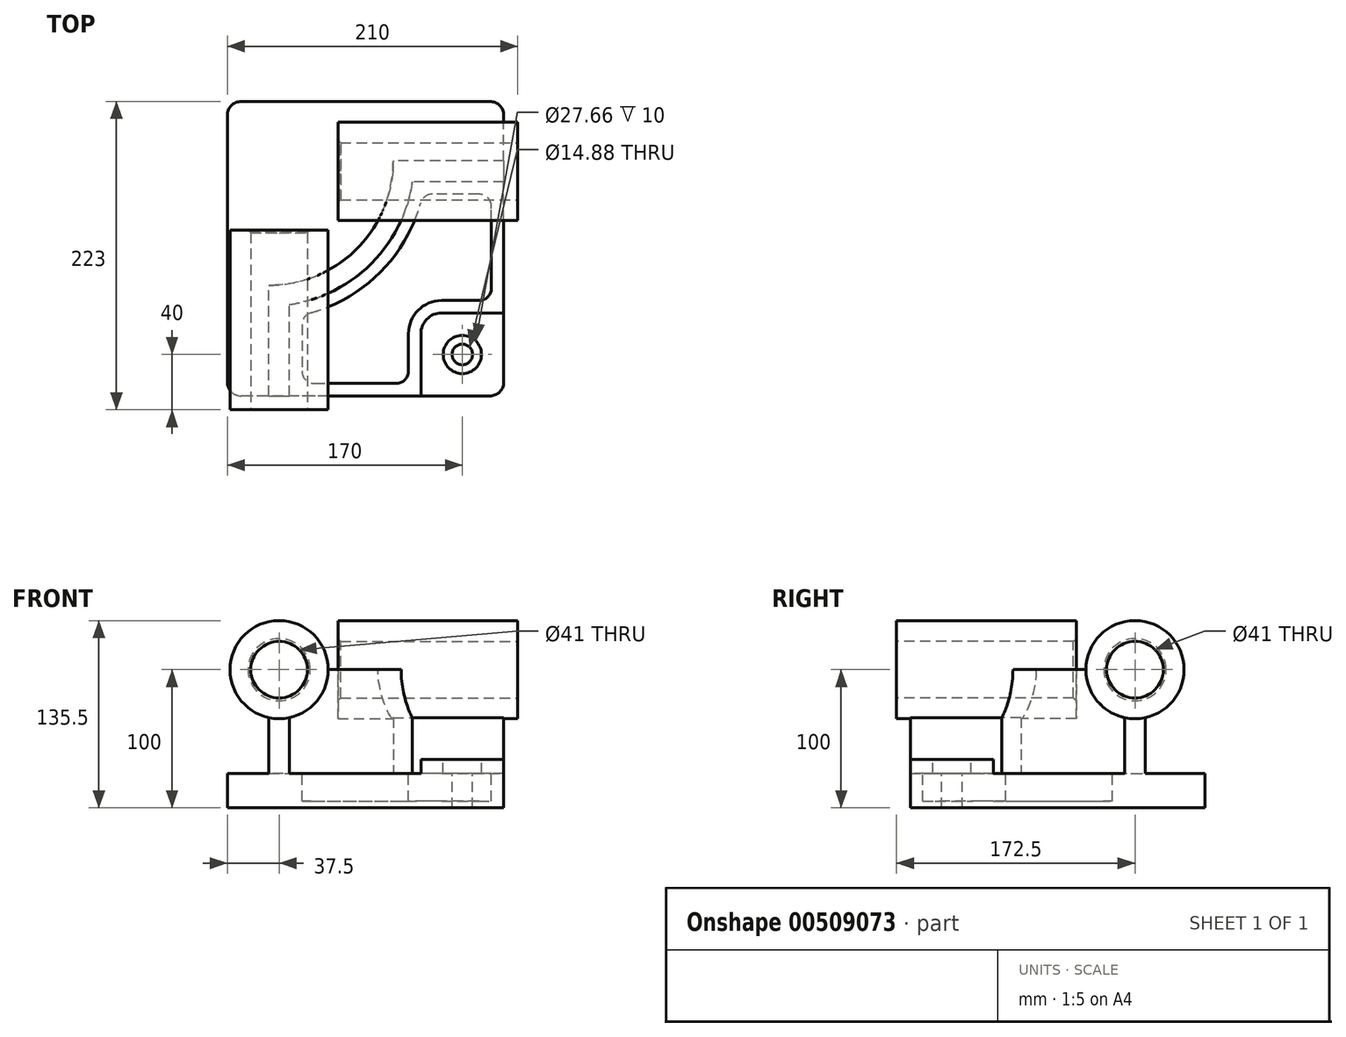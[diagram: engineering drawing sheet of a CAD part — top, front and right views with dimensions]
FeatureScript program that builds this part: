
annotation { "Feature Type Name" : "Feature", "Feature Type Description" : "" }
export const myFeature = defineFeature(function(context is Context, id is Id, definition is map)
    precondition{}
    {
        {
            var Q0;
            Q0=qCreatedBy(makeId("Top.planeOp"),FACE);
            var sketch = newSketch(context, id + "F0", { "sketchPlane" : qUnion([Q0])});
            skLineSegment(sketch, "E0.bottom", {"start": v(-10, 0) * mm, "end": v(-190, 0) * mm});
            skLineSegment(sketch, "E0.top", {"start": v(-10, 213) * mm, "end": v(-190, 213) * mm});
            skLineSegment(sketch, "E0.left", {"start": v(0, 10) * mm, "end": v(0, 203) * mm});
            skLineSegment(sketch, "E0.right", {"start": v(-200, 10) * mm, "end": v(-200, 203) * mm});
            skPoint(sketch, "E1.visualSharp", {"position": v(-200, 213) * mm});
            skArc(sketch, "E1.filletArc", {"start": v(-190, 213) * mm, "mid": v(-197.07, 210.07) * mm, "end": v(-200, 203) * mm});
            skPoint(sketch, "E2.visualSharp", {"position": v(0, 213) * mm});
            skArc(sketch, "E2.filletArc", {"start": v(0, 203) * mm, "mid": v(-2.93, 210.07) * mm, "end": v(-10, 213) * mm});
            skPoint(sketch, "E3.visualSharp", {"position": v(0, 0) * mm});
            skArc(sketch, "E3.filletArc", {"start": v(-10, 0) * mm, "mid": v(-2.93, 2.93) * mm, "end": v(0, 10) * mm});
            skPoint(sketch, "E4.visualSharp", {"position": v(-200, 0) * mm});
            skArc(sketch, "E4.filletArc", {"start": v(-200, 10) * mm, "mid": v(-197.07, 2.93) * mm, "end": v(-190, 0) * mm});
            skSolve(sketch);
        }
        {
            var Q0;
            Q0=makeQuery(id+"F0.imprint","IMPRINT",FACE,{"disambiguationData":[TD([[makeQuery(id+"F0.imprint","IMPRINT",EDGE,{"derivedFrom":sQuery(id+"F0.wireOp",EDGE,"E0.bottom")}),-1.0]])]});
            extrude(context, id + "F1", {"entities" : qUnion([Q0]), "depth" : 25 * mm});
        }
        {
            var Q0;
            Q0=makeQuery(id+"F1.opExtrude","CAP_FACE",FACE,{"disambiguationData":[OSD([sQuery(id+"F0.wireOp",EDGE,"E0.bottom"),sQuery(id+"F0.wireOp",EDGE,"E0.top"),sQuery(id+"F0.wireOp",EDGE,"E0.left"),sQuery(id+"F0.wireOp",EDGE,"E0.right"),sQuery(id+"F0.wireOp",EDGE,"E1.filletArc"),sQuery(id+"F0.wireOp",EDGE,"E2.filletArc"),sQuery(id+"F0.wireOp",EDGE,"E3.filletArc"),sQuery(id+"F0.wireOp",EDGE,"E4.filletArc")])],"isStart":false});
            var sketch = newSketch(context, id + "F2", { "sketchPlane" : qUnion([Q0])});
            skLineSegment(sketch, "E5", {"start": v(0, 170) * mm, "end": v(-80, 170) * mm});
            skLineSegment(sketch, "E6", {"start": v(-170, 0) * mm, "end": v(-170, 80) * mm});
            skLineSegment(sketch, "E7.0", {"start": v(0, 155) * mm, "end": v(-66.08, 155) * mm});
            skLineSegment(sketch, "E8.0", {"start": v(-155, 0) * mm, "end": v(-155, 66.08) * mm});
            skLineSegment(sketch, "E9", {"start": v(-170, 80) * mm, "end": v(-170, 170) * mm, "construction": true});
            skLineSegment(sketch, "E10", {"start": v(-170, 170) * mm, "end": v(-80, 170) * mm, "construction": true});
            skArc(sketch, "E11", {"start": v(-170, 80) * mm, "mid": v(-106.36, 106.36) * mm, "end": v(-80, 170) * mm});
            skArc(sketch, "E12", {"start": v(-155, 66.08) * mm, "mid": v(-95.75, 95.75) * mm, "end": v(-66.08, 155) * mm});
            skSolve(sketch);
        }
        {
            var Q0;
            Q0 = qSketchRegion(id + "F2", true);
            var Q1;
            {var subQ4=sQuery(id+"F2.wireOp",EDGE,"E5");Q1=makeQuery(id+"F2.imprint","IMPRINT",FACE,{"disambiguationData":[TD([[makeQuery(id+"F2.imprint","IMPRINT",EDGE,{"derivedFrom":subQ4}),1.0]])]});}
            extrude(context, id + "F3", {"entities" : qUnion([Q0, Q1]), "operationType" : NewBodyOperationType.ADD, "depth" : 75 * mm});
        }
        {
            var Q0;
            {var subQ0=sQuery(id+"F0.wireOp",EDGE,"E3.filletArc");var subQ1=sQuery(id+"F0.wireOp",EDGE,"E0.left");var subQ2=sQuery(id+"F0.wireOp",EDGE,"E0.bottom");Q0=makeQuery(id+"F3.boolean.opBoolean","SPLIT",FACE,{"disambiguationData":[TD([makeQuery(id+"F1.opExtrude","SWEPT_FACE",FACE,{"disambiguationData":[OSD([subQ0])]})])],"derivedFrom":makeQuery(id+"F1.opExtrude","CAP_FACE",FACE,{"disambiguationData":[OSD([subQ2,sQuery(id+"F0.wireOp",EDGE,"E0.top"),subQ1,sQuery(id+"F0.wireOp",EDGE,"E0.right"),sQuery(id+"F0.wireOp",EDGE,"E1.filletArc"),sQuery(id+"F0.wireOp",EDGE,"E2.filletArc"),subQ0,sQuery(id+"F0.wireOp",EDGE,"E4.filletArc")])],"isStart":false})});}
            var sketch = newSketch(context, id + "F4", { "sketchPlane" : qUnion([Q0])});
            skLineSegment(sketch, "E13.bottom", {"start": v(-45, 60) * mm, "end": v(0, 60) * mm});
            skLineSegment(sketch, "E13.top", {"start": v(-60, 0) * mm, "end": v(-10, 0) * mm});
            skLineSegment(sketch, "E13.left", {"start": v(-60, 45) * mm, "end": v(-60, 0) * mm});
            skLineSegment(sketch, "E13.right", {"start": v(0, 60) * mm, "end": v(0, 10) * mm});
            skPoint(sketch, "E14.visualSharp", {"position": v(0, 0) * mm});
            skArc(sketch, "E14.filletArc", {"start": v(-10, 0) * mm, "mid": v(-2.93, 2.93) * mm, "end": v(0, 10) * mm});
            skPoint(sketch, "E15.visualSharp", {"position": v(-60, 60) * mm});
            skArc(sketch, "E15.filletArc", {"start": v(-45, 60) * mm, "mid": v(-55.6, 55.6) * mm, "end": v(-60, 45) * mm});
            skSolve(sketch);
        }
        {
            var Q0;
            Q0=makeQuery(id+"F4.imprint","IMPRINT",FACE,{"disambiguationData":[TD([[makeQuery(id+"F4.imprint","IMPRINT",EDGE,{"derivedFrom":sQuery(id+"F4.wireOp",EDGE,"E13.bottom")}),-1.0]])]});
            extrude(context, id + "F5", {"entities" : qUnion([Q0]), "operationType" : NewBodyOperationType.ADD, "depth" : 10 * mm});
        }
        {
            var Q0;
            Q0=makeQuery(id+"F5.opExtrude","CAP_FACE",FACE,{"disambiguationData":[OSD([sQuery(id+"F4.wireOp",EDGE,"E13.bottom"),sQuery(id+"F4.wireOp",EDGE,"E13.top"),sQuery(id+"F4.wireOp",EDGE,"E13.left"),sQuery(id+"F4.wireOp",EDGE,"E13.right"),sQuery(id+"F4.wireOp",EDGE,"E14.filletArc"),sQuery(id+"F4.wireOp",EDGE,"E15.filletArc")])],"isStart":false});
            var sketch = newSketch(context, id + "F6", { "sketchPlane" : qUnion([Q0])});
            skSolve(sketch);
        }
        {
            var Q0;
            Q0=makeQuery(id+"F6.imprint","IMPRINT",FACE,{"disambiguationData":[TD([[makeQuery(id+"F6.imprint","IMPRINT",EDGE,{"derivedFrom":makeQuery(id+"F5.opExtrude","CAP_EDGE",EDGE,{"disambiguationData":[OSD([sQuery(id+"F4.wireOp",EDGE,"E13.bottom")])],"isStart":false})}),-1.0]])]});
            var sketch = newSketch(context, id + "F7", { "sketchPlane" : qUnion([Q0])});
            skCircle(sketch, "E16", {"center": v(-30, 30) * mm, "radius": 13.83 * mm});
            skCircle(sketch, "E17", {"center": v(-30, 30) * mm, "radius": 7.44 * mm});
            skSolve(sketch);
        }
        {
            var Q0;
            Q0 = qSketchRegion(id + "F7", true);
            extrude(context, id + "F8", {"entities" : qUnion([Q0]), "operationType" : NewBodyOperationType.REMOVE, "oppositeDirection" : true, "depth" : 10 * mm});
        }
        {
            var Q0;
            Q0=makeQuery(id+"F7.imprint","IMPRINT",FACE,{"disambiguationData":[TD([[makeQuery(id+"F7.imprint","IMPRINT",EDGE,{"derivedFrom":sQuery(id+"F7.wireOp",EDGE,"E17")}),1.0]])]});
            var Q1;
            Q1=sQuery(id+"F7.wireOp",EDGE,"E17");
            extrude(context, id + "F9", {"entities" : qUnion([Q0]), "operationType" : NewBodyOperationType.REMOVE, "surfaceEntities" : qUnion([Q1]), "endBound" : BoundingType.THROUGH_ALL, "oppositeDirection" : true, "depth" : 25 * mm});
        }
        {
            var Q0;
            {var subQ0=sQuery(id+"F0.wireOp",EDGE,"E3.filletArc");var subQ1=sQuery(id+"F0.wireOp",EDGE,"E0.left");var subQ2=sQuery(id+"F0.wireOp",EDGE,"E0.bottom");Q0=makeQuery(id+"F3.boolean.opBoolean","SPLIT",FACE,{"disambiguationData":[TD([makeQuery(id+"F1.opExtrude","SWEPT_FACE",FACE,{"disambiguationData":[OSD([subQ0])]})])],"derivedFrom":makeQuery(id+"F1.opExtrude","CAP_FACE",FACE,{"disambiguationData":[OSD([subQ2,sQuery(id+"F0.wireOp",EDGE,"E0.top"),subQ1,sQuery(id+"F0.wireOp",EDGE,"E0.right"),sQuery(id+"F0.wireOp",EDGE,"E1.filletArc"),sQuery(id+"F0.wireOp",EDGE,"E2.filletArc"),subQ0,sQuery(id+"F0.wireOp",EDGE,"E4.filletArc")])],"isStart":false})});}
            var sketch = newSketch(context, id + "F10", { "sketchPlane" : qUnion([Q0])});
            skArc(sketch, "E18.0.0", {"start": v(-60, 45) * mm, "mid": v(-55.6, 55.6) * mm, "end": v(-45, 60) * mm});
            skLineSegment(sketch, "E18.0.1", {"start": v(-45, 60) * mm, "end": v(0, 60) * mm});
            skLineSegment(sketch, "E18.0.2", {"start": v(0, 60) * mm, "end": v(0, 155) * mm});
            skLineSegment(sketch, "E18.0.3", {"start": v(0, 155) * mm, "end": v(-66.08, 155) * mm});
            skArc(sketch, "E18.0.4", {"start": v(-66.08, 155) * mm, "mid": v(-95.75, 95.75) * mm, "end": v(-155, 66.08) * mm});
            skLineSegment(sketch, "E18.0.5", {"start": v(-155, 66.08) * mm, "end": v(-155, 0) * mm});
            skLineSegment(sketch, "E18.0.6", {"start": v(-155, 0) * mm, "end": v(-60, 0) * mm});
            skLineSegment(sketch, "E18.0.7", {"start": v(-60, 0) * mm, "end": v(-60, 45) * mm});
            skLineSegment(sketch, "E19.0", {"start": v(-69, 18) * mm, "end": v(-69, 45) * mm});
            skLineSegment(sketch, "E19.1", {"start": v(-137, 9) * mm, "end": v(-78, 9) * mm});
            skArc(sketch, "E19.2", {"start": v(-69, 45) * mm, "mid": v(-61.97, 61.97) * mm, "end": v(-45, 69) * mm});
            skLineSegment(sketch, "E19.3", {"start": v(-146, 51.5) * mm, "end": v(-146, 18) * mm});
            skLineSegment(sketch, "E19.4", {"start": v(-45, 69) * mm, "end": v(-18, 69) * mm});
            skLineSegment(sketch, "E19.5", {"start": v(-9, 78) * mm, "end": v(-9, 137) * mm});
            skLineSegment(sketch, "E19.6", {"start": v(-18, 146) * mm, "end": v(-51.5, 146) * mm});
            skArc(sketch, "E19.7", {"start": v(-60.18, 139.41) * mm, "mid": v(-89.39, 89.39) * mm, "end": v(-139.41, 60.18) * mm});
            skPoint(sketch, "E20.visualSharp", {"position": v(-146, 58.55) * mm});
            skArc(sketch, "E20.filletArc", {"start": v(-139.41, 60.18) * mm, "mid": v(-144.17, 56.95) * mm, "end": v(-146, 51.5) * mm});
            skPoint(sketch, "E21.visualSharp", {"position": v(-146, 9) * mm});
            skArc(sketch, "E21.filletArc", {"start": v(-146, 18) * mm, "mid": v(-143.36, 11.64) * mm, "end": v(-137, 9) * mm});
            skPoint(sketch, "E22.visualSharp", {"position": v(-69, 9) * mm});
            skArc(sketch, "E22.filletArc", {"start": v(-78, 9) * mm, "mid": v(-71.64, 11.64) * mm, "end": v(-69, 18) * mm});
            skPoint(sketch, "E23.visualSharp", {"position": v(-9, 69) * mm});
            skArc(sketch, "E23.filletArc", {"start": v(-18, 69) * mm, "mid": v(-11.64, 71.64) * mm, "end": v(-9, 78) * mm});
            skPoint(sketch, "E24.visualSharp", {"position": v(-9, 146) * mm});
            skArc(sketch, "E24.filletArc", {"start": v(-9, 137) * mm, "mid": v(-11.64, 143.36) * mm, "end": v(-18, 146) * mm});
            skPoint(sketch, "E25.visualSharp", {"position": v(-58.55, 146) * mm});
            skArc(sketch, "E25.filletArc", {"start": v(-51.5, 146) * mm, "mid": v(-56.95, 144.17) * mm, "end": v(-60.18, 139.41) * mm});
            skSolve(sketch);
        }
        {
            var Q0;
            Q0=makeQuery(id+"F10.imprint","IMPRINT",FACE,{"disambiguationData":[TD([[makeQuery(id+"F10.imprint","IMPRINT",EDGE,{"derivedFrom":sQuery(id+"F10.wireOp",EDGE,"E19.0")}),1.0]])]});
            extrude(context, id + "F11", {"entities" : qUnion([Q0]), "operationType" : NewBodyOperationType.REMOVE, "oppositeDirection" : true, "depth" : 20 * mm});
        }
        {
            var Q0;
            {var subQ0=sQuery(id+"F0.wireOp",EDGE,"E0.bottom");Q0=makeQuery(id+"F5.boolean.opBoolean","MERGE",FACE,{"derivedFrom":[makeQuery(id+"F3.boolean.opBoolean","MERGE",FACE,{"derivedFrom":[makeQuery(id+"F1.opExtrude","SWEPT_FACE",FACE,{"disambiguationData":[OSD([subQ0])]}),makeQuery(id+"F3.opExtrude","SWEPT_FACE",FACE,{"disambiguationData":[OSD([subQ0])]})]}),makeQuery(id+"F5.opExtrude","SWEPT_FACE",FACE,{"disambiguationData":[OSD([sQuery(id+"F4.wireOp",EDGE,"E13.top")])]})]});}
            cPlane(context, id + "F12", {"entities" : qUnion([Q0]), "cplaneType" : CPlaneType.OFFSET, "offset" : 10 * mm, "width" : 150 * mm, "height" : 150 * mm});
        }
        {
            var Q0;
            Q0=qCreatedBy(id+"F12.planeOp",FACE);
            var sketch = newSketch(context, id + "F13", { "sketchPlane" : qUnion([Q0])});
            skCircle(sketch, "E26", {"center": v(-162.5, 100) * mm, "radius": 35.5 * mm});
            skSolve(sketch);
        }
        {
            var Q0;
            Q0=makeQuery(id+"F13.imprint","IMPRINT",FACE,{"disambiguationData":[TD([[makeQuery(id+"F13.imprint","IMPRINT",EDGE,{"derivedFrom":sQuery(id+"F13.wireOp",EDGE,"E26")}),1.0]])]});
            extrude(context, id + "F14", {"entities" : qUnion([Q0]), "operationType" : NewBodyOperationType.ADD, "oppositeDirection" : true, "depth" : 130 * mm});
        }
        {
            var Q0;
            Q0=makeQuery(id+"F14.opExtrude","CAP_FACE",FACE,{"disambiguationData":[OSD([sQuery(id+"F13.wireOp",EDGE,"E26")])],"isStart":true});
            var sketch = newSketch(context, id + "F15", { "sketchPlane" : qUnion([Q0])});
            skCircle(sketch, "E27", {"center": v(-162.5, 100) * mm, "radius": 20.5 * mm});
            skSolve(sketch);
        }
        {
            var Q0;
            Q0 = qSketchRegion(id + "F15", true);
            extrude(context, id + "F16", {"entities" : qUnion([Q0]), "operationType" : NewBodyOperationType.REMOVE, "endBound" : BoundingType.THROUGH_ALL, "oppositeDirection" : true, "depth" : 25 * mm});
        }
        {
            var Q0;
            {var subQ0=sQuery(id+"F0.wireOp",EDGE,"E0.left");Q0=makeQuery(id+"F5.boolean.opBoolean","MERGE",FACE,{"derivedFrom":[makeQuery(id+"F3.boolean.opBoolean","MERGE",FACE,{"derivedFrom":[makeQuery(id+"F1.opExtrude","SWEPT_FACE",FACE,{"disambiguationData":[OSD([subQ0])]}),makeQuery(id+"F3.opExtrude","SWEPT_FACE",FACE,{"disambiguationData":[OSD([subQ0])]})]}),makeQuery(id+"F5.opExtrude","SWEPT_FACE",FACE,{"disambiguationData":[OSD([sQuery(id+"F4.wireOp",EDGE,"E13.right")])]})]});}
            cPlane(context, id + "F17", {"entities" : qUnion([Q0]), "cplaneType" : CPlaneType.OFFSET, "offset" : 10 * mm, "width" : 150 * mm, "height" : 150 * mm});
        }
        {
            var Q0;
            Q0=qCreatedBy(id+"F17.planeOp",FACE);
            var sketch = newSketch(context, id + "F18", { "sketchPlane" : qUnion([Q0])});
            skCircle(sketch, "E28", {"center": v(162.5, 100) * mm, "radius": 35.5 * mm});
            skSolve(sketch);
        }
        {
            var Q0;
            Q0=makeQuery(id+"F18.imprint","IMPRINT",FACE,{"disambiguationData":[TD([[makeQuery(id+"F18.imprint","IMPRINT",EDGE,{"derivedFrom":sQuery(id+"F18.wireOp",EDGE,"E28")}),1.0]])]});
            extrude(context, id + "F19", {"entities" : qUnion([Q0]), "operationType" : NewBodyOperationType.ADD, "oppositeDirection" : true, "depth" : 130 * mm});
        }
        {
            var Q0;
            Q0=makeQuery(id+"F19.opExtrude","CAP_FACE",FACE,{"disambiguationData":[OSD([sQuery(id+"F18.wireOp",EDGE,"E28")])],"isStart":true});
            var sketch = newSketch(context, id + "F20", { "sketchPlane" : qUnion([Q0])});
            skCircle(sketch, "E29", {"center": v(162.5, 100) * mm, "radius": 20.5 * mm});
            skSolve(sketch);
        }
        {
            var Q0;
            Q0=makeQuery(id+"F20.imprint","IMPRINT",FACE,{"disambiguationData":[TD([[makeQuery(id+"F20.imprint","IMPRINT",EDGE,{"derivedFrom":sQuery(id+"F20.wireOp",EDGE,"E29")}),1.0]])]});
            var Q1;
            Q1=sQuery(id+"F20.wireOp",EDGE,"E29");
            extrude(context, id + "F21", {"entities" : qUnion([Q0]), "operationType" : NewBodyOperationType.REMOVE, "surfaceEntities" : qUnion([Q1]), "endBound" : BoundingType.THROUGH_ALL, "oppositeDirection" : true, "depth" : 25 * mm});
        }
        {
            var Q0;
            Q0=makeQuery(id+"F21.boolean.opBoolean","COPY",EDGE,{"derivedFrom":makeQuery(id+"F21.opExtrude","CAP_EDGE",EDGE,{"disambiguationData":[OSD([sQuery(id+"F20.wireOp",EDGE,"E29")])],"isStart":true})});
            var Q1;
            Q1=makeQuery(id+"F16.boolean.opBoolean","COPY",EDGE,{"derivedFrom":makeQuery(id+"F16.opExtrude","CAP_EDGE",EDGE,{"disambiguationData":[OSD([sQuery(id+"F15.wireOp",EDGE,"E27")])],"isStart":true})});
            var Q2;
            Q2=makeQuery(id+"F21.boolean.opBoolean","INTERSECT",EDGE,{"derivedFrom":[makeQuery(id+"F19.opExtrude","CAP_FACE",FACE,{"disambiguationData":[OSD([sQuery(id+"F18.wireOp",EDGE,"E28")])],"isStart":false}),makeQuery(id+"F21.opExtrude","SWEPT_FACE",FACE,{"disambiguationData":[OSD([sQuery(id+"F20.wireOp",EDGE,"E29")])]})]});
            var Q3;
            Q3=makeQuery(id+"F16.boolean.opBoolean","INTERSECT",EDGE,{"derivedFrom":[makeQuery(id+"F14.opExtrude","CAP_FACE",FACE,{"disambiguationData":[OSD([sQuery(id+"F13.wireOp",EDGE,"E26")])],"isStart":false}),makeQuery(id+"F16.opExtrude","SWEPT_FACE",FACE,{"disambiguationData":[OSD([sQuery(id+"F15.wireOp",EDGE,"E27")])]})]});
            chamfer(context, id + "F22", {"entities" : qUnion([Q0, Q1, Q2, Q3]), "width" : 2 * mm, "tangentPropagation" : true});
        }
    });
